# Revit family: 1Plumbing-Fixture_Mincey-Marble-Manufacturing_SP-CUST-Custom-Shower-Pan
name_source: partatom
category: Plumbing Fixtures
units: mm (PartAtom-declared; Revit-internal decimal feet)

## family parameters
Always vertical = Yes
Cut with Voids When Loaded = No
Maintain Annotation Orientation = No
OmniClass Number = 23.45.05.14.11.21
Part Type = Normal
Room Calculation Point = No
Round Connector Dimension = Use Diameter
Shared = No
Work Plane-Based = No

## types (1)
- SP-CUST - Custom Shower Pan
    Assembly Code = D2010.60
    Default Elevation = 0 "
    Description = Custom Built Shower Pan
    Drain Diameter = 2 "
    Flow = 0 GPM
    Height = 4 "
    Keynote = 22 40 00.B3
    Manufacturer = Mincey Marble Manufacturing
    Model = SP-CUST
    Product Documentation Link = https://minceymarble.com
    Product Page URL = https://minceymarble.com
    URL = https://minceymarble.com
    Vent Connection = No
    Version = 1

## geometry (parser evidence)
native form markers: Sweep x3
no freeform markers — native parametric forms only
